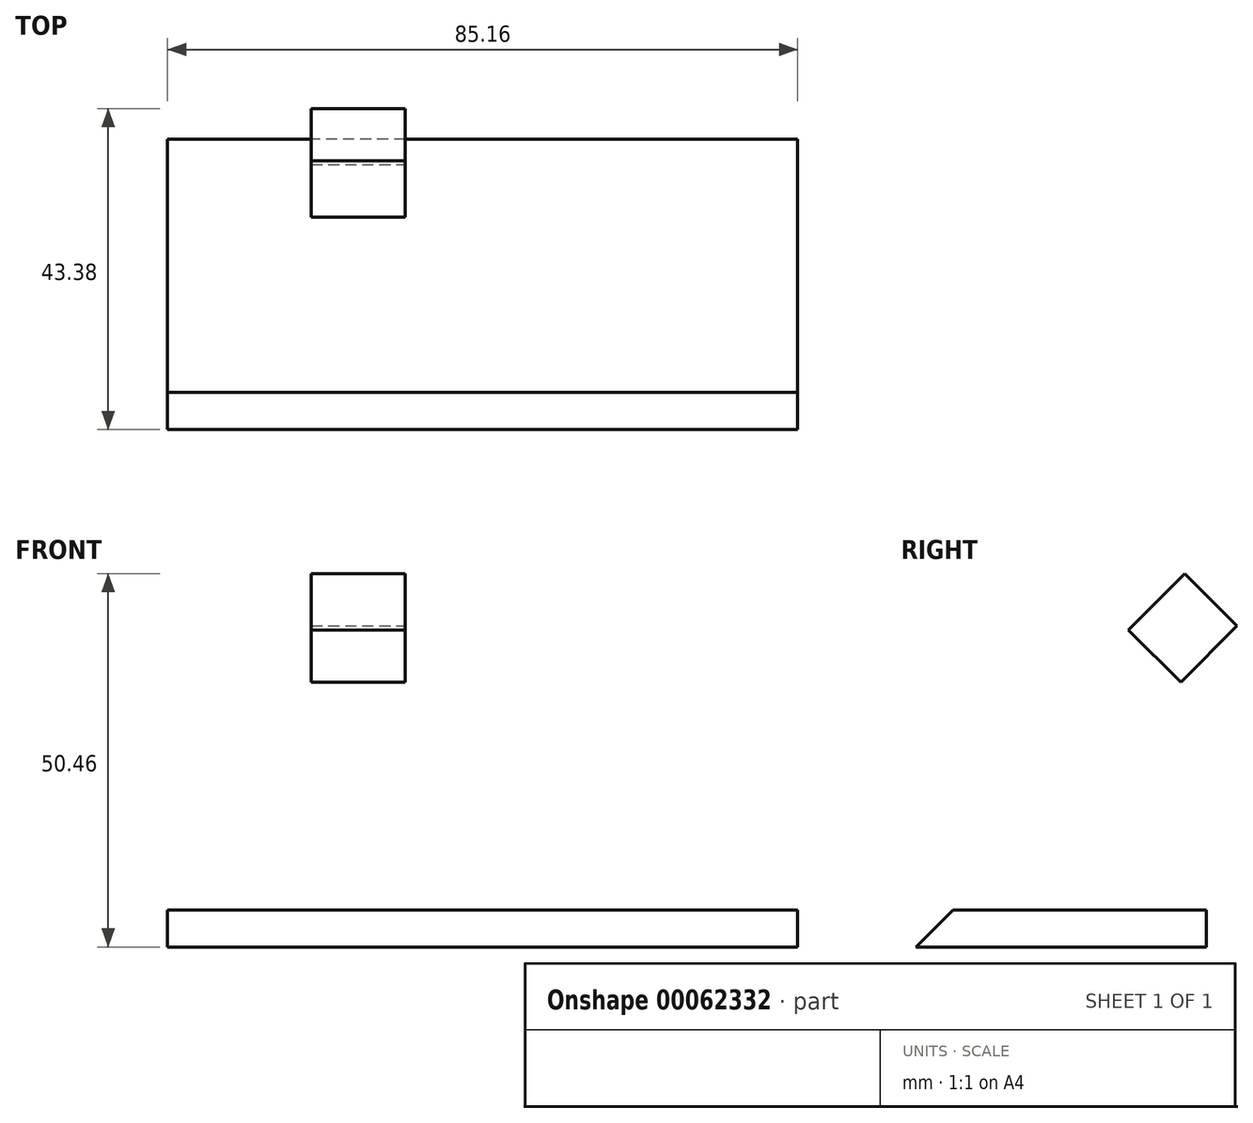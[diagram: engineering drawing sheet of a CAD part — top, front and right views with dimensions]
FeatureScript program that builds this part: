
annotation { "Feature Type Name" : "Feature", "Feature Type Description" : "" }
export const myFeature = defineFeature(function(context is Context, id is Id, definition is map)
    precondition{}
    {
        {
            var Q0;
            Q0=qCreatedBy(makeId("Top.planeOp"),FACE);
            var sketch = newSketch(context, id + "F0", { "sketchPlane" : qUnion([Q0])});
            skLineSegment(sketch, "E0.rect.bottom", {"start": v(42.58, -19.63) * mm, "end": v(-42.58, -19.63) * mm});
            skLineSegment(sketch, "E0.rect.top", {"start": v(42.58, 19.63) * mm, "end": v(-42.58, 19.63) * mm});
            skLineSegment(sketch, "E0.rect.left", {"start": v(42.58, -19.63) * mm, "end": v(42.58, 19.63) * mm});
            skLineSegment(sketch, "E0.rect.right", {"start": v(-42.58, -19.63) * mm, "end": v(-42.58, 19.63) * mm});
            skPoint(sketch, "E0.rect.middle", {"position": v(0, 0) * mm});
            skSolve(sketch);
        }
        {
            var Q0;
            Q0=makeQuery(id+"F0.imprint","IMPRINT",FACE,{"disambiguationData":[TD([[makeQuery(id+"F0.imprint","IMPRINT",EDGE,{"derivedFrom":sQuery(id+"F0.wireOp",EDGE,"E0.rect.bottom")}),-1.0]])]});
            extrude(context, id + "F1", {"entities" : qUnion([Q0]), "depth" : 5 * mm});
        }
        {
            var Q0;
            Q0=makeQuery(id+"F1.opExtrude","CAP_EDGE",EDGE,{"disambiguationData":[OSD([sQuery(id+"F0.wireOp",EDGE,"E0.rect.bottom")])],"isStart":false});
            chamfer(context, id + "F2", {"entities" : qUnion([Q0]), "width" : 5 * mm, "tangentPropagation" : true});
        }
        {
            var Q0;
            Q0=makeQuery(id+"F2.opChamfer","BLEND_FACE",FACE,{"disambiguationData":[OSD([sQuery(id+"F0.wireOp",EDGE,"E0.rect.bottom")])]});
            var sketch = newSketch(context, id + "F3", { "sketchPlane" : qUnion([Q0])});
            skLineSegment(sketch, "E1.bottom", {"start": v(-23.15, 36.73) * mm, "end": v(-10.45, 36.73) * mm});
            skLineSegment(sketch, "E1.top", {"start": v(-23.15, 47.47) * mm, "end": v(-10.45, 47.47) * mm});
            skLineSegment(sketch, "E1.left", {"start": v(-23.15, 36.73) * mm, "end": v(-23.15, 47.47) * mm});
            skLineSegment(sketch, "E1.right", {"start": v(-10.45, 36.73) * mm, "end": v(-10.45, 47.47) * mm});
            skSolve(sketch);
        }
        {
            var Q0;
            Q0=makeQuery(id+"F3.imprint","IMPRINT",FACE,{"disambiguationData":[TD([[makeQuery(id+"F3.imprint","IMPRINT",EDGE,{"derivedFrom":sQuery(id+"F3.wireOp",EDGE,"E1.bottom")}),1.0]])]});
            extrude(context, id + "F4", {"entities" : qUnion([Q0]), "depth" : 10 * mm});
        }
        {
            var Q0;
            Q0=makeQuery(id+"F4.opExtrude","SWEPT_FACE",FACE,{"disambiguationData":[OSD([sQuery(id+"F3.wireOp",EDGE,"E1.top")])]});
            var sketch = newSketch(context, id + "F5", { "sketchPlane" : qUnion([Q0])});
            skPoint(sketch, "E2", {"position": v(13.7, 18.63) * mm});
            skSolve(sketch);
        }
    });
